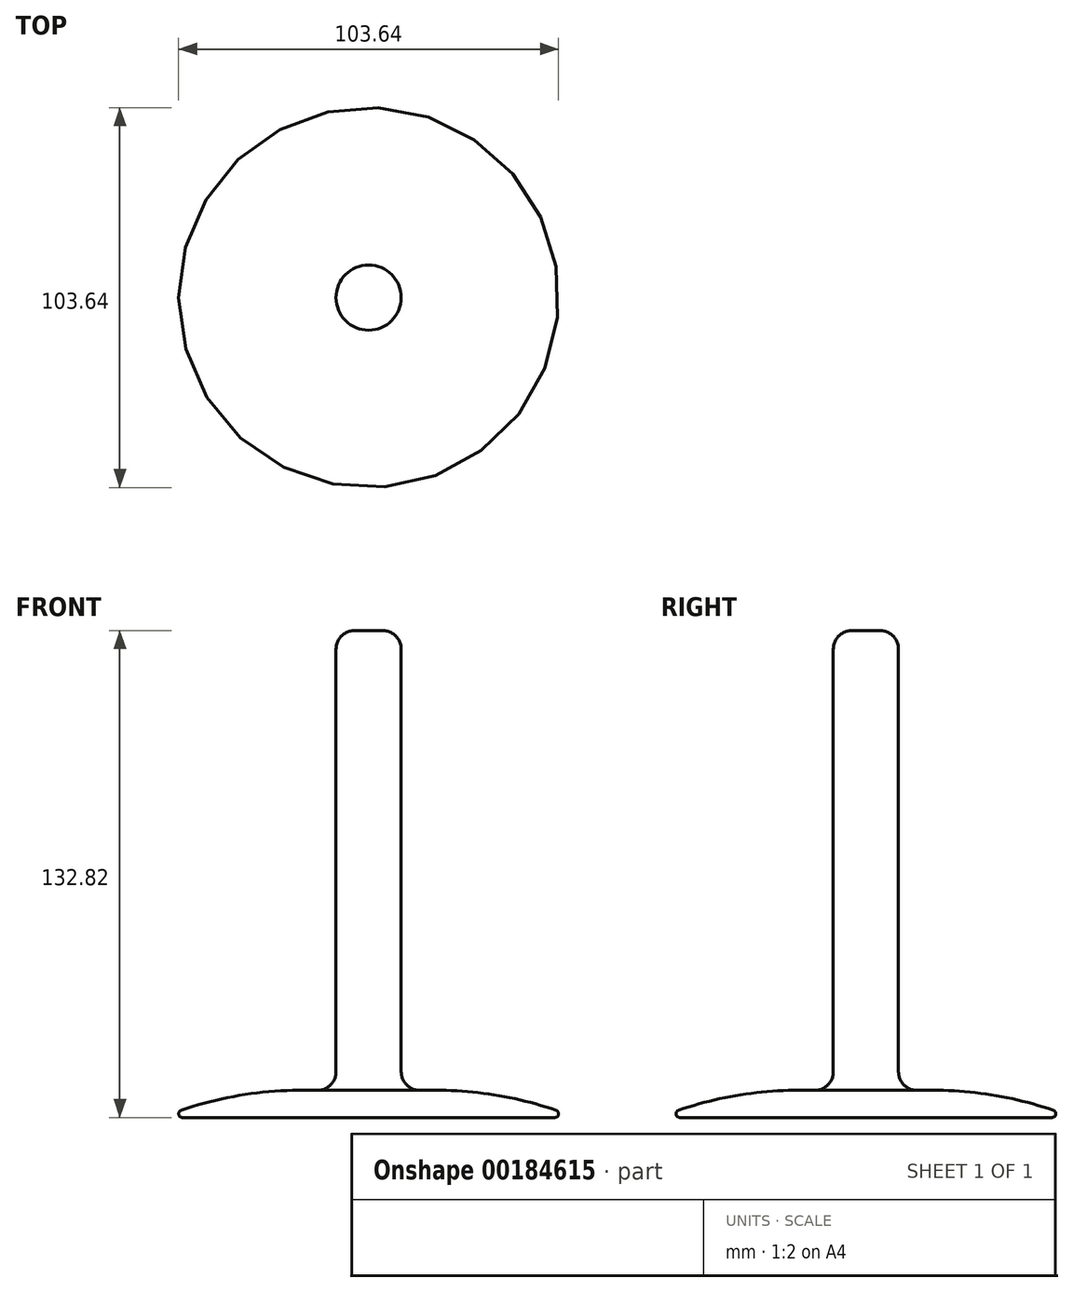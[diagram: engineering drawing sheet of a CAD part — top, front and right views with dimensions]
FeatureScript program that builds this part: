
annotation { "Feature Type Name" : "Feature", "Feature Type Description" : "" }
export const myFeature = defineFeature(function(context is Context, id is Id, definition is map)
    precondition{}
    {
        {
            var Q0;
            Q0=qCreatedBy(makeId("Top.planeOp"),FACE);
            var sketch = newSketch(context, id + "F0", { "sketchPlane" : qUnion([Q0])});
            skCircle(sketch, "E0", {"center": v(0, 0) * mm, "radius": 8.9 * mm});
            skSolve(sketch);
        }
        {
            var Q0;
            Q0 = qSketchRegion(id + "F0", true);
            extrude(context, id + "F1", {"entities" : qUnion([Q0]), "depth" : 127 * mm});
        }
        {
            var Q0;
            Q0=qCreatedBy(makeId("Right.planeOp"),FACE);
            var sketch = newSketch(context, id + "F2", { "sketchPlane" : qUnion([Q0])});
            skLineSegment(sketch, "E1", {"start": v(0, -5.82) * mm, "end": v(-50.8, -5.82) * mm});
            skLineSegment(sketch, "E2", {"start": v(0, -27.68) * mm, "end": v(0, 25.04) * mm, "construction": true});
            skArc(sketch, "E3", {"start": v(-51.13, -3.85) * mm, "mid": v(-25.81, 1.36) * mm, "end": v(0, 0) * mm});
            skPoint(sketch, "E4.visualSharp", {"position": v(-56.41, -5.82) * mm});
            skArc(sketch, "E4.filletArc", {"start": v(-51.13, -3.85) * mm, "mid": v(-51.8, -4.97) * mm, "end": v(-50.8, -5.82) * mm});
            skLineSegment(sketch, "E5", {"start": v(0, -5.82) * mm, "end": v(0, 0) * mm});
            skSolve(sketch);
        }
        {
            var Q0;
            Q0 = qSketchRegion(id + "F2", true);
            var Q1;
            Q1=sQuery(id+"F2.wireOp",EDGE,"E2");
            revolve(context, id + "F3", {"operationType" : NewBodyOperationType.ADD, "entities" : qUnion([Q0]), "axis" : qUnion([Q1]), "revolveType" : RevolveType.FULL});
        }
        {
            var Q0;
            Q0=makeQuery(id+"F1.opExtrude","CAP_EDGE",EDGE,{"disambiguationData":[OSD([sQuery(id+"F0.wireOp",EDGE,"E0")])],"isStart":false});
            var Q1;
            Q1=makeQuery(id+"F3.boolean.opBoolean","INTERSECT",EDGE,{"derivedFrom":[makeQuery(id+"F1.opExtrude","SWEPT_FACE",FACE,{"disambiguationData":[OSD([sQuery(id+"F0.wireOp",EDGE,"E0")])]}),makeQuery(id+"F3.opRevolve","SWEPT_FACE",FACE,{"disambiguationData":[OSD([sQuery(id+"F2.wireOp",EDGE,"E3")])]})]});
            fillet(context, id + "F4", {"entities" : qUnion([Q0, Q1]), "radius" : 5.08 * mm, "tangentPropagation" : true, "allowEdgeOverflow" : false});
        }
    });
